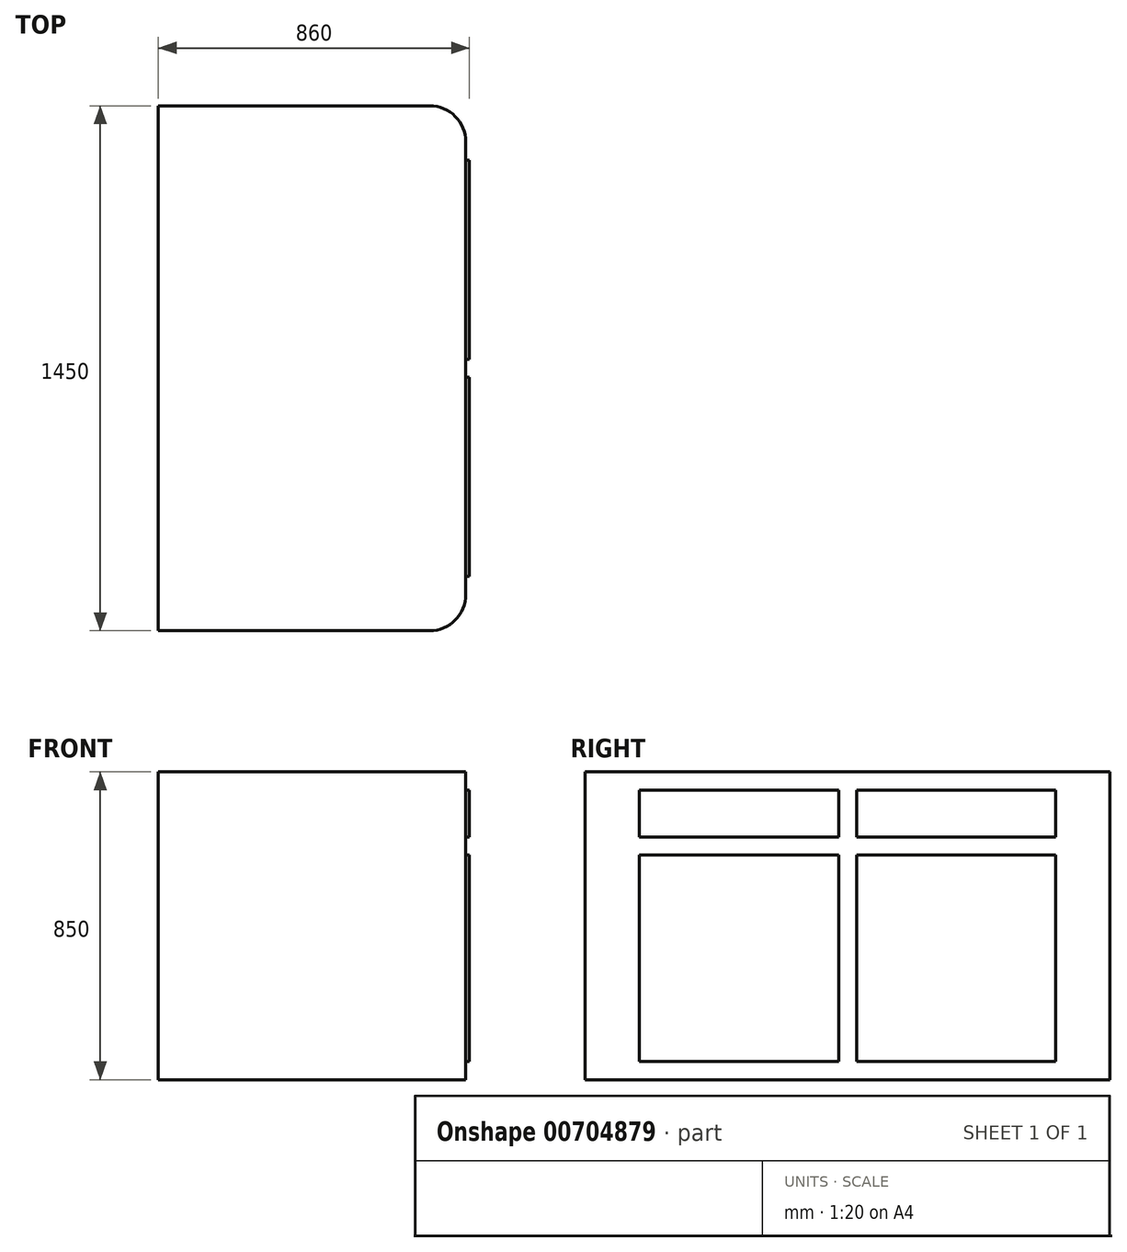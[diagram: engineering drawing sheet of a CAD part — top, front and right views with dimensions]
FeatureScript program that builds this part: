
annotation { "Feature Type Name" : "Feature", "Feature Type Description" : "" }
export const myFeature = defineFeature(function(context is Context, id is Id, definition is map)
    precondition{}
    {
        {
            var Q0;
            Q0=qCreatedBy(makeId("Top.planeOp"),FACE);
            var sketch = newSketch(context, id + "F0", { "sketchPlane" : qUnion([Q0])});
            skLineSegment(sketch, "E0.bottom", {"start": v(0, 0) * mm, "end": v(750, 0) * mm});
            skLineSegment(sketch, "E0.top", {"start": v(0, 1450) * mm, "end": v(750, 1450) * mm});
            skLineSegment(sketch, "E0.left", {"start": v(0, 0) * mm, "end": v(0, 1450) * mm});
            skLineSegment(sketch, "E0.right", {"start": v(850, 100) * mm, "end": v(850, 1350) * mm});
            skPoint(sketch, "E1.visualSharp", {"position": v(850, 1450) * mm});
            skArc(sketch, "E1.filletArc", {"start": v(850, 1350) * mm, "mid": v(820.71, 1420.71) * mm, "end": v(750, 1450) * mm});
            skPoint(sketch, "E2.visualSharp", {"position": v(850, 0) * mm});
            skArc(sketch, "E2.filletArc", {"start": v(750, 0) * mm, "mid": v(820.71, 29.29) * mm, "end": v(850, 100) * mm});
            skSolve(sketch);
        }
        {
            var Q0;
            Q0=makeQuery(id+"F0.imprint","IMPRINT",FACE,{"disambiguationData":[TD([[makeQuery(id+"F0.imprint","IMPRINT",EDGE,{"derivedFrom":sQuery(id+"F0.wireOp",EDGE,"E0.bottom")}),1.0]])]});
            extrude(context, id + "F1", {"entities" : qUnion([Q0]), "depth" : 850 * mm, "offsetDistance" : 25 * mm});
        }
        {
            var Q0;
            Q0=makeQuery(id+"F1.opExtrude","SWEPT_FACE",FACE,{"disambiguationData":[OSD([sQuery(id+"F0.wireOp",EDGE,"E0.right")])]});
            var sketch = newSketch(context, id + "F2", { "sketchPlane" : qUnion([Q0])});
            skLineSegment(sketch, "E3.bottom", {"start": v(150, 800) * mm, "end": v(700, 800) * mm});
            skLineSegment(sketch, "E3.top", {"start": v(150, 670) * mm, "end": v(700, 670) * mm});
            skLineSegment(sketch, "E3.left", {"start": v(150, 800) * mm, "end": v(150, 670) * mm});
            skLineSegment(sketch, "E3.right", {"start": v(700, 800) * mm, "end": v(700, 670) * mm});
            skLineSegment(sketch, "E4.bottom", {"start": v(750, 800) * mm, "end": v(1300, 800) * mm});
            skLineSegment(sketch, "E4.top", {"start": v(750, 670) * mm, "end": v(1300, 670) * mm});
            skLineSegment(sketch, "E4.left", {"start": v(750, 800) * mm, "end": v(750, 670) * mm});
            skLineSegment(sketch, "E4.right", {"start": v(1300, 800) * mm, "end": v(1300, 670) * mm});
            skLineSegment(sketch, "E5.bottom", {"start": v(150, 620) * mm, "end": v(700, 620) * mm});
            skLineSegment(sketch, "E5.top", {"start": v(150, 50) * mm, "end": v(700, 50) * mm});
            skLineSegment(sketch, "E5.left", {"start": v(150, 620) * mm, "end": v(150, 50) * mm});
            skLineSegment(sketch, "E5.right", {"start": v(700, 620) * mm, "end": v(700, 50) * mm});
            skLineSegment(sketch, "E6.bottom", {"start": v(750, 620) * mm, "end": v(1300, 620) * mm});
            skLineSegment(sketch, "E6.top", {"start": v(750, 50) * mm, "end": v(1300, 50) * mm});
            skLineSegment(sketch, "E6.left", {"start": v(750, 620) * mm, "end": v(750, 50) * mm});
            skLineSegment(sketch, "E6.right", {"start": v(1300, 620) * mm, "end": v(1300, 50) * mm});
            skSolve(sketch);
        }
        {
            var Q0;
            Q0=makeQuery(id+"F2.imprint","IMPRINT",FACE,{"disambiguationData":[TD([[makeQuery(id+"F2.imprint","IMPRINT",EDGE,{"derivedFrom":sQuery(id+"F2.wireOp",EDGE,"E3.bottom")}),-1.0]])]});
            var Q1;
            Q1=makeQuery(id+"F2.imprint","IMPRINT",FACE,{"disambiguationData":[TD([[makeQuery(id+"F2.imprint","IMPRINT",EDGE,{"derivedFrom":sQuery(id+"F2.wireOp",EDGE,"E4.bottom")}),-1.0]])]});
            var Q2;
            Q2=makeQuery(id+"F2.imprint","IMPRINT",FACE,{"disambiguationData":[TD([[makeQuery(id+"F2.imprint","IMPRINT",EDGE,{"derivedFrom":sQuery(id+"F2.wireOp",EDGE,"E5.bottom")}),-1.0]])]});
            var Q3;
            Q3=makeQuery(id+"F2.imprint","IMPRINT",FACE,{"disambiguationData":[TD([[makeQuery(id+"F2.imprint","IMPRINT",EDGE,{"derivedFrom":sQuery(id+"F2.wireOp",EDGE,"E6.bottom")}),-1.0]])]});
            extrude(context, id + "F3", {"entities" : qUnion([Q0, Q1, Q2, Q3]), "operationType" : NewBodyOperationType.ADD, "depth" : 10 * mm, "offsetDistance" : 25 * mm});
        }
    });
